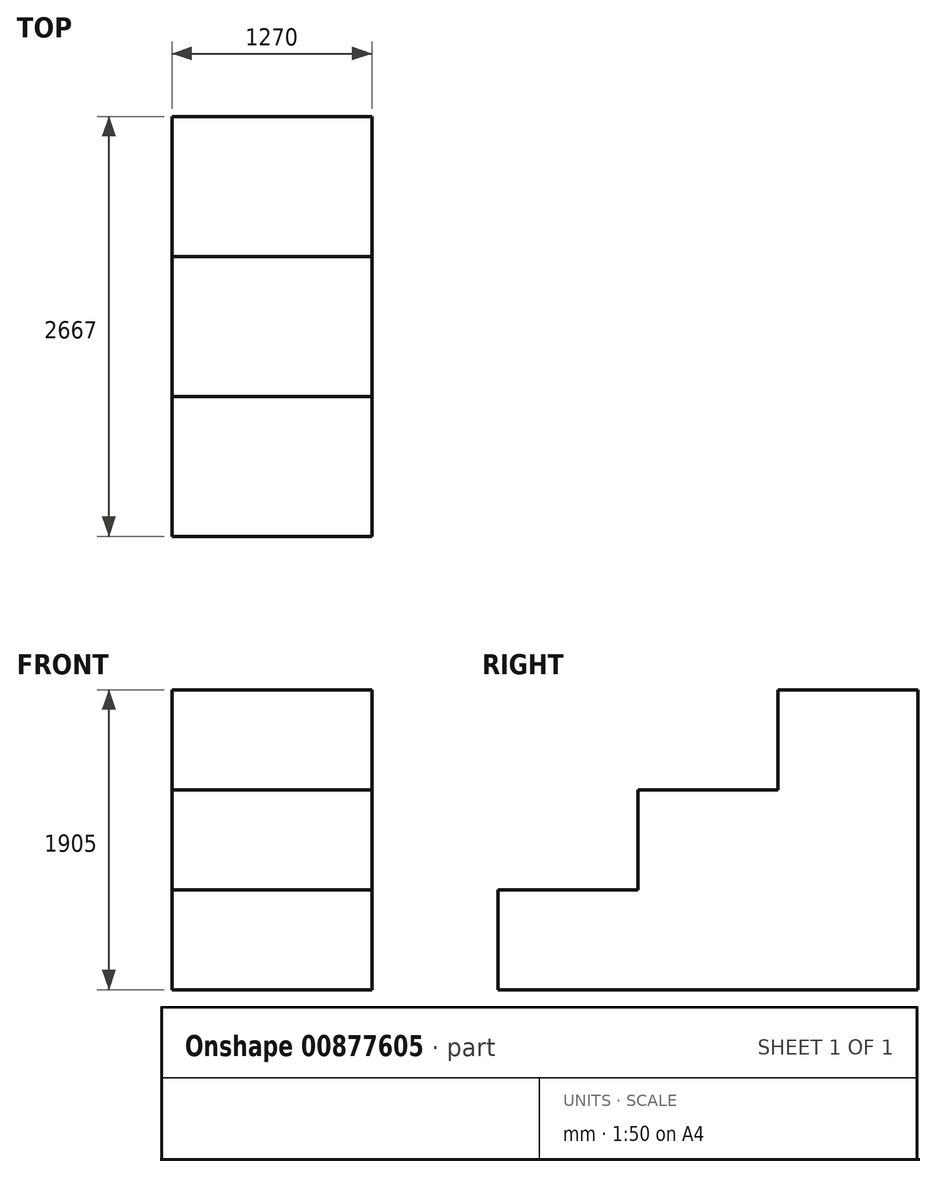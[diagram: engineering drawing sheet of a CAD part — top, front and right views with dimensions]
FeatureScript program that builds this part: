
annotation { "Feature Type Name" : "Feature", "Feature Type Description" : "" }
export const myFeature = defineFeature(function(context is Context, id is Id, definition is map)
    precondition{}
    {
        {
            var Q0;
            Q0=qCreatedBy(makeId("Top.planeOp"),FACE);
            var sketch = newSketch(context, id + "F0", { "sketchPlane" : qUnion([Q0])});
            skLineSegment(sketch, "E0.bottom", {"start": v(0, 0) * mm, "end": v(-1270, 0) * mm});
            skLineSegment(sketch, "E0.top", {"start": v(0, -2667) * mm, "end": v(-1270, -2667) * mm});
            skLineSegment(sketch, "E0.left", {"start": v(0, 0) * mm, "end": v(0, -2667) * mm});
            skLineSegment(sketch, "E0.right", {"start": v(-1270, 0) * mm, "end": v(-1270, -2667) * mm});
            skSolve(sketch);
        }
        {
            var Q0;
            Q0=makeQuery(id+"F0.imprint","IMPRINT",FACE,{"disambiguationData":[TD([[makeQuery(id+"F0.imprint","IMPRINT",EDGE,{"derivedFrom":sQuery(id+"F0.wireOp",EDGE,"E0.bottom")}),1.0]])]});
            extrude(context, id + "F1", {"entities" : qUnion([Q0]), "depth" : 1905 * mm, "offsetDistance" : 25.4 * mm});
        }
        {
            var Q0;
            Q0=makeQuery(id+"F1.opExtrude","SWEPT_FACE",FACE,{"disambiguationData":[OSD([sQuery(id+"F0.wireOp",EDGE,"E0.left")])]});
            var sketch = newSketch(context, id + "F2", { "sketchPlane" : qUnion([Q0])});
            skLineSegment(sketch, "E1", {"start": v(-2667, 0) * mm, "end": v(-2667, 635) * mm});
            skLineSegment(sketch, "E2", {"start": v(-2667, 635) * mm, "end": v(-1778, 635) * mm});
            skLineSegment(sketch, "E3", {"start": v(-1778, 635) * mm, "end": v(-1778, 1270) * mm});
            skLineSegment(sketch, "E4", {"start": v(-1778, 1270) * mm, "end": v(-889, 1270) * mm});
            skLineSegment(sketch, "E5", {"start": v(-889, 1270) * mm, "end": v(-889, 1905) * mm});
            skSolve(sketch);
        }
        {
            var Q0;
            {var subQ1=sQuery(id+"F2.wireOp",EDGE,"E2");Q0=makeQuery(id+"F2.imprint","IMPRINT",FACE,{"disambiguationData":[TD([[makeQuery(id+"F2.imprint","IMPRINT",EDGE,{"derivedFrom":subQ1}),1.0]])]});}
            extrude(context, id + "F3", {"entities" : qUnion([Q0]), "operationType" : NewBodyOperationType.REMOVE, "oppositeDirection" : true, "depth" : 1739.9 * mm, "offsetDistance" : 25.4 * mm});
        }
    });
